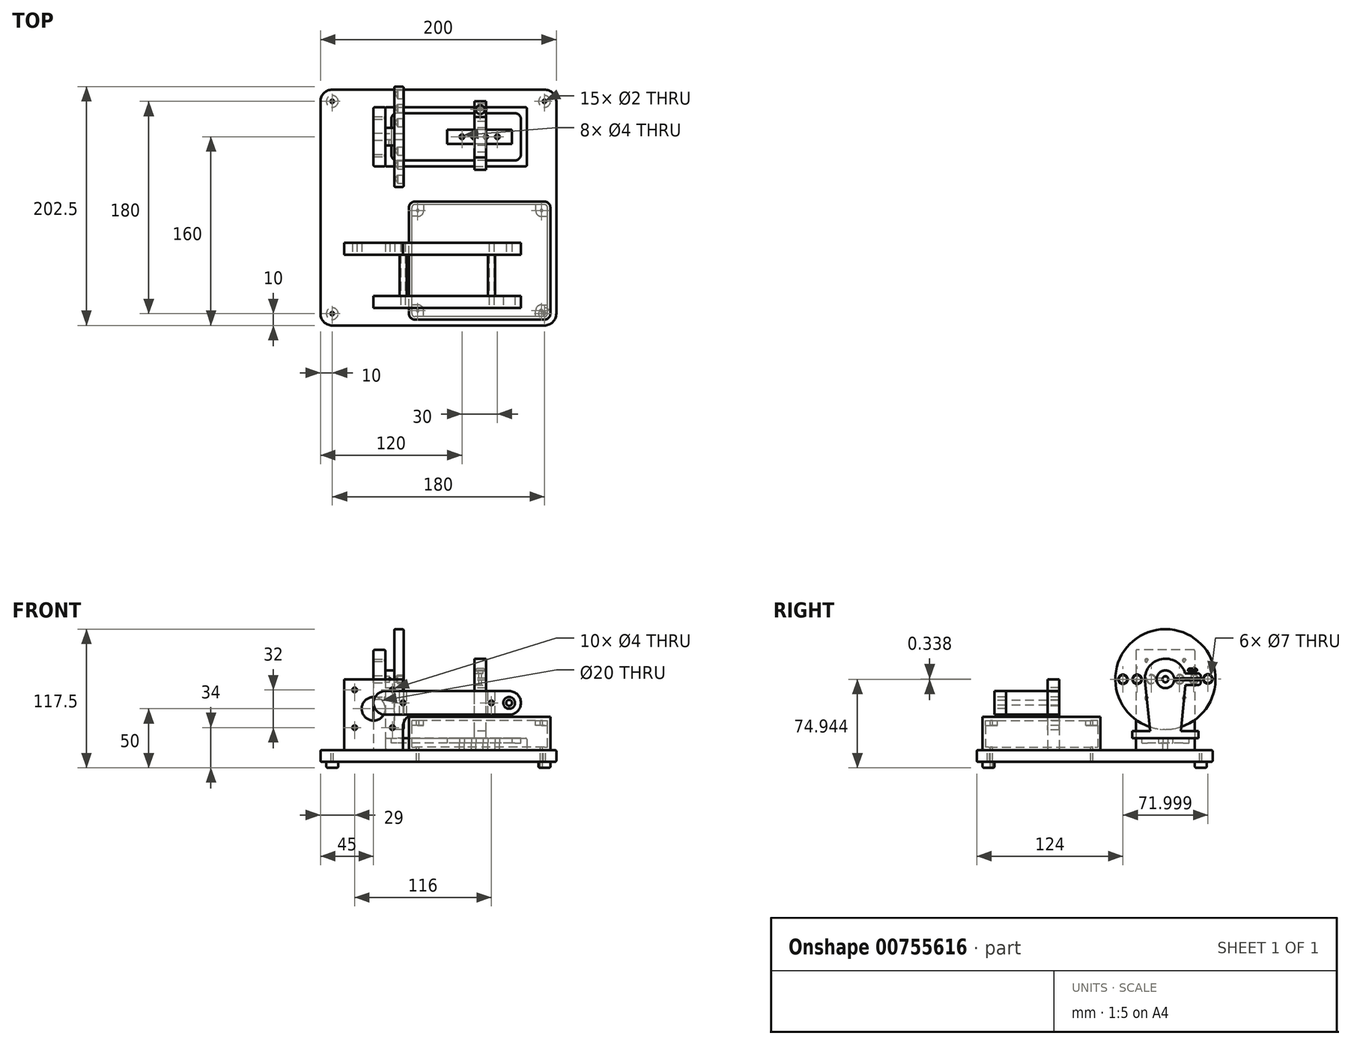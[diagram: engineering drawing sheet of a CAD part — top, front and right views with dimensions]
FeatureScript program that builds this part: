
annotation { "Feature Type Name" : "Feature", "Feature Type Description" : "" }
export const myFeature = defineFeature(function(context is Context, id is Id, definition is map)
    precondition{}
    {
        {
            var Q0;
            Q0=qCreatedBy(makeId("Top.planeOp"),FACE);
            var sketch = newSketch(context, id + "F0", { "sketchPlane" : qUnion([Q0])});
            skLineSegment(sketch, "E0.bottom", {"start": v(100, -100) * mm, "end": v(-100, -100) * mm});
            skLineSegment(sketch, "E0.top", {"start": v(100, 100) * mm, "end": v(-100, 100) * mm});
            skLineSegment(sketch, "E0.left", {"start": v(100, -100) * mm, "end": v(100, 100) * mm});
            skLineSegment(sketch, "E0.right", {"start": v(-100, -100) * mm, "end": v(-100, 100) * mm});
            skPoint(sketch, "E0.middle", {"position": v(0, 0) * mm});
            skSolve(sketch);
        }
        {
            var Q0;
            Q0=makeQuery(id+"F0.imprint","IMPRINT",FACE,{"disambiguationData":[TD([[makeQuery(id+"F0.imprint","IMPRINT",EDGE,{"derivedFrom":sQuery(id+"F0.wireOp",EDGE,"E0.bottom")}),-1.0]])]});
            extrude(context, id + "F1", {"entities" : qUnion([Q0]), "depth" : 10 * mm, "offsetDistance" : 25.4 * mm});
        }
        {
            var Q0;
            Q0=makeQuery(id+"F1.opExtrude","SWEPT_EDGE",EDGE,{"disambiguationData":[OSD([sQuery(id+"F0.wireOp",EDGE,"E0.bottom"),sQuery(id+"F0.wireOp",EDGE,"E0.left")])]});
            var Q1;
            Q1=makeQuery(id+"F1.opExtrude","SWEPT_EDGE",EDGE,{"disambiguationData":[OSD([sQuery(id+"F0.wireOp",EDGE,"E0.top"),sQuery(id+"F0.wireOp",EDGE,"E0.left")])]});
            var Q2;
            Q2=makeQuery(id+"F1.opExtrude","SWEPT_EDGE",EDGE,{"disambiguationData":[OSD([sQuery(id+"F0.wireOp",EDGE,"E0.top"),sQuery(id+"F0.wireOp",EDGE,"E0.right")])]});
            var Q3;
            Q3=makeQuery(id+"F1.opExtrude","SWEPT_EDGE",EDGE,{"disambiguationData":[OSD([sQuery(id+"F0.wireOp",EDGE,"E0.bottom"),sQuery(id+"F0.wireOp",EDGE,"E0.right")])]});
            fillet(context, id + "F2", {"entities" : qUnion([Q0, Q1, Q2, Q3]), "radius" : 10 * mm, "tangentPropagation" : true, "allowEdgeOverflow" : false});
        }
        {
            var Q0;
            Q0=makeQuery(id+"F1.opExtrude","CAP_FACE",FACE,{"disambiguationData":[OSD([sQuery(id+"F0.wireOp",EDGE,"E0.bottom"),sQuery(id+"F0.wireOp",EDGE,"E0.top"),sQuery(id+"F0.wireOp",EDGE,"E0.left"),sQuery(id+"F0.wireOp",EDGE,"E0.right")])],"isStart":false});
            var sketch = newSketch(context, id + "F3", { "sketchPlane" : qUnion([Q0])});
            skLineSegment(sketch, "E1.bottom", {"start": v(90, -90) * mm, "end": v(-90, -90) * mm, "construction": true});
            skLineSegment(sketch, "E1.top", {"start": v(90, 90) * mm, "end": v(-90, 90) * mm, "construction": true});
            skLineSegment(sketch, "E1.left", {"start": v(90, -90) * mm, "end": v(90, 90) * mm, "construction": true});
            skLineSegment(sketch, "E1.right", {"start": v(-90, -90) * mm, "end": v(-90, 90) * mm, "construction": true});
            skPoint(sketch, "E1.middle", {"position": v(0, 0) * mm});
            skSolve(sketch);
        }
        {
            var Q0;
            Q0=sQuery(id+"F3.wireOp",VERTEX,"E1.right.end");
            var Q1;
            Q1=sQuery(id+"F3.wireOp",VERTEX,"E1.left.end");
            var Q2;
            Q2=sQuery(id+"F3.wireOp",VERTEX,"E1.bottom.start");
            var Q3;
            Q3=sQuery(id+"F3.wireOp",VERTEX,"E1.right.start");
            var Q4;
            Q4=makeQuery(id+"F1.opExtrude","SWEPT_BODY",BODY,{"disambiguationData":[OSD([sQuery(id+"F0.wireOp",EDGE,"E0.bottom"),sQuery(id+"F0.wireOp",EDGE,"E0.top"),sQuery(id+"F0.wireOp",EDGE,"E0.left"),sQuery(id+"F0.wireOp",EDGE,"E0.right")])]});
            hole(context, id + "F4", {"style" : HoleStyle.C_SINK, "endStyle" : HoleEndStyle.THROUGH, "holeDiameter" : 2 * mm, "cSinkDiameter" : 3 * mm, "cSinkAngle" : 82 * degree, "majorDiameter" : 5 * mm, "isTappedThrough" : true, "tappedDepth" : 12 * mm, "tapClearance" : 3, "locations" : qUnion([Q0, Q1, Q2, Q3]), "scope" : qUnion([Q4])});
        }
        {
            var Q0;
            Q0=sQuery(id+"F3.wireOp",EDGE,"E1.left");
            var Q1;
            Q1=sQuery(id+"F3.wireOp",VERTEX,"E1.bottom.start");
            cPlane(context, id + "F5", {"entities" : qUnion([Q0, Q1]), "cplaneType" : CPlaneType.LINE_POINT, "offset" : 25 * mm, "width" : 150 * mm, "height" : 150 * mm});
        }
        {
            var Q0;
            Q0=qCreatedBy(id+"F5.planeOp",FACE);
            var sketch = newSketch(context, id + "F6", { "sketchPlane" : qUnion([Q0])});
            skLineSegment(sketch, "E2", {"start": v(-90, 10) * mm, "end": v(-90, -5) * mm, "construction": true});
            skLineSegment(sketch, "E3", {"start": v(-90, -5) * mm, "end": v(-95, -5) * mm});
            skLineSegment(sketch, "E4", {"start": v(-95, -5) * mm, "end": v(-95, 0) * mm});
            skLineSegment(sketch, "E5", {"start": v(-95, 0) * mm, "end": v(-90, 0) * mm});
            skLineSegment(sketch, "E6", {"start": v(-90, 0) * mm, "end": v(-90, -5) * mm});
            skSolve(sketch);
        }
        {
            var Q0;
            Q0=makeQuery(id+"F6.imprint","IMPRINT",FACE,{"disambiguationData":[TD([[makeQuery(id+"F6.imprint","IMPRINT",EDGE,{"derivedFrom":sQuery(id+"F6.wireOp",EDGE,"E3")}),-1.0]])]});
            var Q1;
            Q1=sQuery(id+"F6.wireOp",EDGE,"E6");
            revolve(context, id + "F7", {"surfaceOperationType" : NewSurfaceOperationType.NEW, "entities" : qUnion([Q0]), "axis" : qUnion([Q1]), "revolveType" : RevolveType.FULL});
        }
        {
            var Q0;
            Q0=makeQuery(id+"F7.opRevolve","SWEPT_EDGE",EDGE,{"disambiguationData":[OSD([sQuery(id+"F6.wireOp",EDGE,"E3"),sQuery(id+"F6.wireOp",EDGE,"E4")])]});
            fillet(context, id + "F8", {"entities" : qUnion([Q0]), "radius" : 1 * mm, "tangentPropagation" : true, "allowEdgeOverflow" : false});
        }
        {
            var Q0;
            Q0=makeQuery(id+"F7.opRevolve","SWEPT_BODY",BODY,{"disambiguationData":[OSD([sQuery(id+"F6.wireOp",EDGE,"E3"),sQuery(id+"F6.wireOp",EDGE,"E4"),sQuery(id+"F6.wireOp",EDGE,"E5"),sQuery(id+"F6.wireOp",EDGE,"E6")])]});
            var Q1;
            Q1=qCreatedBy(makeId("Right.planeOp"),FACE);
            mirror(context, id + "F9", {"entities" : qUnion([Q0]), "mirrorPlane" : qUnion([Q1])});
        }
        {
            var Q0;
            Q0=makeQuery(id+"F7.opRevolve","SWEPT_BODY",BODY,{"disambiguationData":[OSD([sQuery(id+"F6.wireOp",EDGE,"E3"),sQuery(id+"F6.wireOp",EDGE,"E4"),sQuery(id+"F6.wireOp",EDGE,"E5"),sQuery(id+"F6.wireOp",EDGE,"E6")])]});
            var Q1;
            Q1=makeQuery(id+"F9.opPattern","COPY",BODY,{"derivedFrom":makeQuery(id+"F7.opRevolve","SWEPT_BODY",BODY,{"disambiguationData":[OSD([sQuery(id+"F6.wireOp",EDGE,"E3"),sQuery(id+"F6.wireOp",EDGE,"E4"),sQuery(id+"F6.wireOp",EDGE,"E5"),sQuery(id+"F6.wireOp",EDGE,"E6")])]}),"instanceName":"1"});
            var Q2;
            Q2=qCreatedBy(makeId("Front.planeOp"),FACE);
            mirror(context, id + "F10", {"entities" : qUnion([Q0, Q1]), "mirrorPlane" : qUnion([Q2])});
        }
        {
            var Q0;
            Q0=makeQuery(id+"F1.opExtrude","CAP_EDGE",EDGE,{"disambiguationData":[OSD([sQuery(id+"F0.wireOp",EDGE,"E0.bottom")])],"isStart":false});
            var Q1;
            Q1=makeQuery(id+"F1.opExtrude","CAP_EDGE",EDGE,{"disambiguationData":[OSD([sQuery(id+"F0.wireOp",EDGE,"E0.bottom")])],"isStart":true});
            fillet(context, id + "F11", {"entities" : qUnion([Q0, Q1]), "radius" : 1 * mm, "tangentPropagation" : true, "allowEdgeOverflow" : false});
        }
        {
            var Q0;
            {var subQ3=sQuery(id+"F0.wireOp",EDGE,"E0.bottom");Q0=makeQuery(id+"F3.imprint","IMPRINT",FACE,{"disambiguationData":[TD([[makeQuery(id+"F3.imprint","IMPRINT",EDGE,{"derivedFrom":makeQuery(id+"F1.opExtrude","CAP_EDGE",EDGE,{"disambiguationData":[OSD([subQ3])],"isStart":false})}),-1.0]])]});}
            var sketch = newSketch(context, id + "F12", { "sketchPlane" : qUnion([Q0])});
            skLineSegment(sketch, "E7.bottom", {"start": v(-55, 85) * mm, "end": v(-45, 85) * mm});
            skLineSegment(sketch, "E7.top", {"start": v(-55, 35) * mm, "end": v(-45, 35) * mm});
            skLineSegment(sketch, "E7.left", {"start": v(-55, 85) * mm, "end": v(-55, 35) * mm});
            skLineSegment(sketch, "E7.right", {"start": v(-45, 85) * mm, "end": v(-45, 35) * mm});
            skSolve(sketch);
        }
        {
            var Q0;
            Q0=makeQuery(id+"F12.imprint","IMPRINT",FACE,{"disambiguationData":[TD([[makeQuery(id+"F12.imprint","IMPRINT",EDGE,{"derivedFrom":sQuery(id+"F12.wireOp",EDGE,"E7.bottom")}),-1.0]])]});
            extrude(context, id + "F13", {"entities" : qUnion([Q0]), "depth" : 85 * mm, "offsetDistance" : 25 * mm});
        }
        {
            var Q0;
            Q0=makeQuery(id+"F13.opExtrude","SWEPT_FACE",FACE,{"disambiguationData":[OSD([sQuery(id+"F12.wireOp",EDGE,"E7.right")])]});
            var sketch = newSketch(context, id + "F14", { "sketchPlane" : qUnion([Q0])});
            skLineSegment(sketch, "E8.bottom", {"start": v(76, 86) * mm, "end": v(44, 86) * mm, "construction": true});
            skLineSegment(sketch, "E8.top", {"start": v(76, 54) * mm, "end": v(44, 54) * mm, "construction": true});
            skLineSegment(sketch, "E8.left", {"start": v(76, 86) * mm, "end": v(76, 54) * mm, "construction": true});
            skLineSegment(sketch, "E8.right", {"start": v(44, 86) * mm, "end": v(44, 54) * mm, "construction": true});
            skPoint(sketch, "E8.middle", {"position": v(60, 70) * mm});
            skPoint(sketch, "E8.middle.positionSnap0", {"position": v(60, 95) * mm});
            skPoint(sketch, "E8.centerSnap0", {"position": v(60, 95) * mm});
            skSolve(sketch);
        }
        {
            var Q0;
            Q0=sQuery(id+"F14.wireOp",VERTEX,"E8.bottom.end");
            var Q1;
            Q1=sQuery(id+"F14.wireOp",VERTEX,"E8.right.end");
            var Q2;
            Q2=sQuery(id+"F14.wireOp",VERTEX,"E8.left.end");
            var Q3;
            Q3=sQuery(id+"F14.wireOp",VERTEX,"E8.left.start");
            var Q4;
            Q4=makeQuery(id+"F13.opExtrude","SWEPT_BODY",BODY,{"disambiguationData":[OSD([sQuery(id+"F12.wireOp",EDGE,"E7.bottom"),sQuery(id+"F12.wireOp",EDGE,"E7.top"),sQuery(id+"F12.wireOp",EDGE,"E7.left"),sQuery(id+"F12.wireOp",EDGE,"E7.right")])]});
            hole(context, id + "F15", {"style" : HoleStyle.C_SINK, "endStyle" : HoleEndStyle.THROUGH, "holeDiameter" : 2 * mm, "cSinkDiameter" : 3 * mm, "cSinkAngle" : 82 * degree, "majorDiameter" : 5 * mm, "isTappedThrough" : true, "tappedDepth" : 12 * mm, "tapClearance" : 3, "locations" : qUnion([Q0, Q1, Q2, Q3]), "scope" : qUnion([Q4])});
        }
        {
            var Q0;
            Q0=sQuery(id+"F14.wireOp",VERTEX,"E8.middle");
            var Q1;
            Q1=makeQuery(id+"F13.opExtrude","SWEPT_BODY",BODY,{"disambiguationData":[OSD([sQuery(id+"F12.wireOp",EDGE,"E7.bottom"),sQuery(id+"F12.wireOp",EDGE,"E7.top"),sQuery(id+"F12.wireOp",EDGE,"E7.left"),sQuery(id+"F12.wireOp",EDGE,"E7.right")])]});
            hole(context, id + "F16", {"style" : HoleStyle.SIMPLE, "endStyle" : HoleEndStyle.BLIND, "holeDiameter" : 6 * mm, "majorDiameter" : 5 * mm, "holeDepth" : 50.8 * mm, "isTappedThrough" : true, "tappedDepth" : 12 * mm, "tapClearance" : 3, "locations" : qUnion([Q0]), "scope" : qUnion([Q1])});
        }
        {
            var Q0;
            Q0=makeQuery(id+"F13.opExtrude","SWEPT_FACE",FACE,{"disambiguationData":[OSD([sQuery(id+"F12.wireOp",EDGE,"E7.top")])]});
            cPlane(context, id + "F17", {"entities" : qUnion([Q0]), "cplaneType" : CPlaneType.OFFSET, "offset" : 25 * mm, "oppositeDirection" : true, "width" : 150 * mm, "height" : 150 * mm});
        }
        {
            var Q0;
            Q0=qCreatedBy(id+"F17.planeOp",FACE);
            var sketch = newSketch(context, id + "F18", { "sketchPlane" : qUnion([Q0])});
            skLineSegment(sketch, "E9.bottom", {"start": v(-45, 62.5) * mm, "end": v(-52.5, 62.5) * mm, "construction": true});
            skLineSegment(sketch, "E9.top", {"start": v(-37.5, 77.5) * mm, "end": v(-52.5, 77.5) * mm, "construction": true});
            skLineSegment(sketch, "E9.left", {"start": v(-37.5, 62.5) * mm, "end": v(-37.5, 77.5) * mm, "construction": true});
            skLineSegment(sketch, "E9.right", {"start": v(-52.5, 62.5) * mm, "end": v(-52.5, 77.5) * mm, "construction": true});
            skPoint(sketch, "E9.middle", {"position": v(-45, 70) * mm});
            skLineSegment(sketch, "E10", {"start": v(-37.5, 77.5) * mm, "end": v(-45, 77.5) * mm});
            skLineSegment(sketch, "E11", {"start": v(-45, 77.5) * mm, "end": v(-45, 70) * mm});
            skLineSegment(sketch, "E12", {"start": v(-45, 62.5) * mm, "end": v(-37.5, 62.5) * mm});
            skLineSegment(sketch, "E13", {"start": v(-37.5, 77.5) * mm, "end": v(-37.5, 112.5) * mm});
            skLineSegment(sketch, "E14", {"start": v(-37.5, 112.5) * mm, "end": v(-29.5, 112.5) * mm});
            skLineSegment(sketch, "E15", {"start": v(-29.5, 112.5) * mm, "end": v(-29.5, 70) * mm});
            skLineSegment(sketch, "E16", {"start": v(-45, 70) * mm, "end": v(-29.5, 70) * mm});
            skPoint(sketch, "E17.end.orphan", {"position": v(-35, 27.5) * mm});
            skPoint(sketch, "E17.start.orphan", {"position": v(-29.5, 27.5) * mm});
            skSolve(sketch);
        }
        {
            var Q0;
            Q0=makeQuery(id+"F18.imprint","IMPRINT",FACE,{"disambiguationData":[TD([[makeQuery(id+"F18.imprint","IMPRINT",EDGE,{"derivedFrom":sQuery(id+"F18.wireOp",EDGE,"E10")}),1.0]])]});
            var Q1;
            Q1=sQuery(id+"F18.wireOp",EDGE,"E16");
            revolve(context, id + "F19", {"surfaceOperationType" : NewSurfaceOperationType.NEW, "entities" : qUnion([Q0]), "axis" : qUnion([Q1]), "revolveType" : RevolveType.FULL});
        }
        {
            var Q0;
            Q0=sQuery(id+"F14.wireOp",VERTEX,"E8.middle");
            var Q1;
            Q1=makeQuery(id+"F19.opRevolve","SWEPT_BODY",BODY,{"disambiguationData":[OSD([sQuery(id+"F18.wireOp",EDGE,"E10"),sQuery(id+"F18.wireOp",EDGE,"E11"),sQuery(id+"F18.wireOp",EDGE,"E13"),sQuery(id+"F18.wireOp",EDGE,"E14"),sQuery(id+"F18.wireOp",EDGE,"E15"),sQuery(id+"F18.wireOp",EDGE,"E16")])]});
            hole(context, id + "F20", {"style" : HoleStyle.SIMPLE, "endStyle" : HoleEndStyle.BLIND, "oppositeDirection" : true, "holeDiameter" : 5 * mm, "majorDiameter" : 5 * mm, "holeDepth" : 50.8 * mm, "isTappedThrough" : true, "tappedDepth" : 12 * mm, "tapClearance" : 3, "locations" : qUnion([Q0]), "scope" : qUnion([Q1])});
        }
        {
            var Q0;
            Q0=makeQuery(id+"F19.opRevolve","SWEPT_FACE",FACE,{"disambiguationData":[OSD([sQuery(id+"F18.wireOp",EDGE,"E15")])]});
            var sketch = newSketch(context, id + "F21", { "sketchPlane" : qUnion([Q0])});
            skLineSegment(sketch, "E18", {"start": v(48, 69.94) * mm, "end": v(60, 70) * mm, "construction": true});
            skLineSegment(sketch, "E19", {"start": v(48, 69.94) * mm, "end": v(36, 69.94) * mm, "construction": true});
            skLineSegment(sketch, "E20", {"start": v(36, 69.94) * mm, "end": v(24, 69.94) * mm, "construction": true});
            skLineSegment(sketch, "E21", {"start": v(60, 70) * mm, "end": v(59.93, 85.7) * mm, "construction": true});
            skLineSegment(sketch, "E22.MirrorCS", {"start": v(72, 70.06) * mm, "end": v(60, 70) * mm, "construction": true});
            skLineSegment(sketch, "E23.MirrorCS", {"start": v(72, 70.06) * mm, "end": v(84, 70.17) * mm, "construction": true});
            skLineSegment(sketch, "E24.MirrorCS", {"start": v(84, 70.17) * mm, "end": v(96, 70.28) * mm, "construction": true});
            skSolve(sketch);
        }
        {
            var Q0;
            Q0=sQuery(id+"F21.wireOp",VERTEX,"E20.end");
            var Q1;
            Q1=sQuery(id+"F21.wireOp",VERTEX,"E18.start");
            var Q2;
            Q2=sQuery(id+"F21.wireOp",VERTEX,"E23.MirrorCS.start");
            var Q3;
            Q3=sQuery(id+"F21.wireOp",VERTEX,"E24.MirrorCS.start");
            var Q4;
            Q4=sQuery(id+"F21.wireOp",VERTEX,"E24.MirrorCS.end");
            var Q5;
            Q5=sQuery(id+"F21.wireOp",VERTEX,"E19.end");
            var Q6;
            Q6=makeQuery(id+"F19.opRevolve","SWEPT_BODY",BODY,{"disambiguationData":[OSD([sQuery(id+"F18.wireOp",EDGE,"E10"),sQuery(id+"F18.wireOp",EDGE,"E11"),sQuery(id+"F18.wireOp",EDGE,"E13"),sQuery(id+"F18.wireOp",EDGE,"E14"),sQuery(id+"F18.wireOp",EDGE,"E15"),sQuery(id+"F18.wireOp",EDGE,"E16")])]});
            hole(context, id + "F22", {"style" : HoleStyle.C_SINK, "endStyle" : HoleEndStyle.BLIND, "holeDiameter" : 7 * mm, "cSinkDiameter" : 8 * mm, "cSinkAngle" : 82 * degree, "majorDiameter" : 5 * mm, "holeDepth" : 5 * mm, "isTappedThrough" : true, "tappedDepth" : 12 * mm, "tapClearance" : 3, "locations" : qUnion([Q0, Q1, Q2, Q3, Q4, Q5]), "scope" : qUnion([Q6])});
        }
        {
            var Q0;
            Q0=qCreatedBy(id+"F17.planeOp",FACE);
            var sketch = newSketch(context, id + "F23", { "sketchPlane" : qUnion([Q0])});
            skLineSegment(sketch, "E25", {"start": v(-45, 70) * mm, "end": v(-41.25, 70) * mm, "construction": true});
            skSolve(sketch);
        }
        {
            var Q0;
            Q0=qCreatedBy(id+"F17.planeOp",FACE);
            cPlane(context, id + "F24", {"entities" : qUnion([Q0]), "cplaneType" : CPlaneType.OFFSET, "offset" : 10 * mm, "width" : 150 * mm, "height" : 150 * mm});
        }
        {
            var Q0;
            Q0=qCreatedBy(id+"F24.planeOp",FACE);
            var sketch = newSketch(context, id + "F25", { "sketchPlane" : qUnion([Q0])});
            skPoint(sketch, "E26", {"position": v(-41.25, 70) * mm});
            skSolve(sketch);
        }
        {
            var Q0;
            Q0=sQuery(id+"F25.wireOp",VERTEX,"E26");
            var Q1;
            Q1=makeQuery(id+"F19.opRevolve","SWEPT_BODY",BODY,{"disambiguationData":[OSD([sQuery(id+"F18.wireOp",EDGE,"E10"),sQuery(id+"F18.wireOp",EDGE,"E11"),sQuery(id+"F18.wireOp",EDGE,"E13"),sQuery(id+"F18.wireOp",EDGE,"E14"),sQuery(id+"F18.wireOp",EDGE,"E15"),sQuery(id+"F18.wireOp",EDGE,"E16")])]});
            hole(context, id + "F26", {"style" : HoleStyle.SIMPLE, "endStyle" : HoleEndStyle.BLIND, "holeDiameter" : 2 * mm, "majorDiameter" : 5 * mm, "holeDepth" : 5 * mm, "isTappedThrough" : true, "tappedDepth" : 12 * mm, "tapClearance" : 3, "locations" : qUnion([Q0]), "scope" : qUnion([Q1])});
        }
        {
            var Q0;
            Q0=makeQuery(id+"F19.opRevolve","SWEPT_EDGE",EDGE,{"disambiguationData":[OSD([sQuery(id+"F18.wireOp",EDGE,"E14"),sQuery(id+"F18.wireOp",EDGE,"E15")])]});
            var Q1;
            Q1=makeQuery(id+"F19.opRevolve","SWEPT_EDGE",EDGE,{"disambiguationData":[OSD([sQuery(id+"F18.wireOp",EDGE,"E13"),sQuery(id+"F18.wireOp",EDGE,"E14")])]});
            fillet(context, id + "F27", {"entities" : qUnion([Q0, Q1]), "radius" : 1 * mm, "tangentPropagation" : true, "allowEdgeOverflow" : false});
        }
        {
            var Q0;
            Q0=makeQuery(id+"F13.opExtrude","SWEPT_EDGE",EDGE,{"disambiguationData":[OSD([sQuery(id+"F12.wireOp",EDGE,"E7.top"),sQuery(id+"F12.wireOp",EDGE,"E7.right")])]});
            var Q1;
            Q1=makeQuery(id+"F13.opExtrude","SWEPT_EDGE",EDGE,{"disambiguationData":[OSD([sQuery(id+"F12.wireOp",EDGE,"E7.top"),sQuery(id+"F12.wireOp",EDGE,"E7.left")])]});
            var Q2;
            Q2=makeQuery(id+"F13.opExtrude","SWEPT_EDGE",EDGE,{"disambiguationData":[OSD([sQuery(id+"F12.wireOp",EDGE,"E7.bottom"),sQuery(id+"F12.wireOp",EDGE,"E7.left")])]});
            var Q3;
            Q3=makeQuery(id+"F13.opExtrude","SWEPT_EDGE",EDGE,{"disambiguationData":[OSD([sQuery(id+"F12.wireOp",EDGE,"E7.bottom"),sQuery(id+"F12.wireOp",EDGE,"E7.right")])]});
            var Q4;
            Q4=makeQuery(id+"F13.opExtrude","CAP_EDGE",EDGE,{"disambiguationData":[OSD([sQuery(id+"F12.wireOp",EDGE,"E7.bottom")])],"isStart":false});
            var Q5;
            Q5=makeQuery(id+"F13.opExtrude","CAP_EDGE",EDGE,{"disambiguationData":[OSD([sQuery(id+"F12.wireOp",EDGE,"E7.left")])],"isStart":false});
            var Q6;
            Q6=makeQuery(id+"F13.opExtrude","CAP_EDGE",EDGE,{"disambiguationData":[OSD([sQuery(id+"F12.wireOp",EDGE,"E7.right")])],"isStart":false});
            var Q7;
            Q7=makeQuery(id+"F13.opExtrude","CAP_EDGE",EDGE,{"disambiguationData":[OSD([sQuery(id+"F12.wireOp",EDGE,"E7.top")])],"isStart":false});
            fillet(context, id + "F28", {"entities" : qUnion([Q0, Q1, Q2, Q3, Q4, Q5, Q6, Q7]), "radius" : 1 * mm, "tangentPropagation" : true, "allowEdgeOverflow" : false});
        }
        {
            var Q0;
            Q0=makeQuery(id+"F12.imprint","IMPRINT",FACE,{"disambiguationData":[TD([[makeQuery(id+"F12.imprint","IMPRINT",EDGE,{"derivedFrom":sQuery(id+"F12.wireOp",EDGE,"E7.bottom")}),1.0]])]});
            var sketch = newSketch(context, id + "F29", { "sketchPlane" : qUnion([Q0])});
            skLineSegment(sketch, "E27.bottom", {"start": v(-45, 85) * mm, "end": v(75, 85) * mm});
            skLineSegment(sketch, "E27.top", {"start": v(-45, 35) * mm, "end": v(75, 35) * mm});
            skLineSegment(sketch, "E27.left", {"start": v(-45, 85) * mm, "end": v(-45, 35) * mm});
            skLineSegment(sketch, "E27.right", {"start": v(75, 85) * mm, "end": v(75, 35) * mm});
            skSolve(sketch);
        }
        {
            var Q0;
            Q0 = qSketchRegion(id + "F29", true);
            extrude(context, id + "F30", {"entities" : qUnion([Q0]), "depth" : 10 * mm, "offsetDistance" : 25 * mm});
        }
        {
            var Q0;
            Q0=makeQuery(id+"F30.opExtrude","CAP_FACE",FACE,{"disambiguationData":[OSD([sQuery(id+"F29.wireOp",EDGE,"E27.bottom"),sQuery(id+"F29.wireOp",EDGE,"E27.top"),sQuery(id+"F29.wireOp",EDGE,"E27.left"),sQuery(id+"F29.wireOp",EDGE,"E27.right")])],"isStart":false});
            var sketch = newSketch(context, id + "F31", { "sketchPlane" : qUnion([Q0])});
            skLineSegment(sketch, "E28.bottom", {"start": v(70, 80) * mm, "end": v(-40, 80) * mm});
            skLineSegment(sketch, "E28.top", {"start": v(70, 40) * mm, "end": v(-40, 40) * mm});
            skLineSegment(sketch, "E28.left", {"start": v(70, 80) * mm, "end": v(70, 40) * mm});
            skLineSegment(sketch, "E28.right", {"start": v(-40, 80) * mm, "end": v(-40, 40) * mm});
            skSolve(sketch);
        }
        {
            var Q0;
            Q0=makeQuery(id+"F31.imprint","IMPRINT",FACE,{"disambiguationData":[TD([[makeQuery(id+"F31.imprint","IMPRINT",EDGE,{"derivedFrom":sQuery(id+"F31.wireOp",EDGE,"E28.bottom")}),1.0]])]});
            extrude(context, id + "F32", {"entities" : qUnion([Q0]), "operationType" : NewBodyOperationType.REMOVE, "oppositeDirection" : true, "depth" : 4 * mm, "offsetDistance" : 25 * mm});
        }
        {
            var Q0;
            Q0=makeQuery(id+"F32.boolean.opBoolean","COPY",EDGE,{"derivedFrom":makeQuery(id+"F32.opExtrude","SWEPT_EDGE",EDGE,{"disambiguationData":[OSD([sQuery(id+"F31.wireOp",EDGE,"E28.top"),sQuery(id+"F31.wireOp",EDGE,"E28.right")])]})});
            var Q1;
            Q1=makeQuery(id+"F32.boolean.opBoolean","COPY",EDGE,{"derivedFrom":makeQuery(id+"F32.opExtrude","SWEPT_EDGE",EDGE,{"disambiguationData":[OSD([sQuery(id+"F31.wireOp",EDGE,"E28.bottom"),sQuery(id+"F31.wireOp",EDGE,"E28.right")])]})});
            var Q2;
            Q2=makeQuery(id+"F32.boolean.opBoolean","COPY",EDGE,{"derivedFrom":makeQuery(id+"F32.opExtrude","SWEPT_EDGE",EDGE,{"disambiguationData":[OSD([sQuery(id+"F31.wireOp",EDGE,"E28.bottom"),sQuery(id+"F31.wireOp",EDGE,"E28.left")])]})});
            var Q3;
            Q3=makeQuery(id+"F32.boolean.opBoolean","COPY",EDGE,{"derivedFrom":makeQuery(id+"F32.opExtrude","SWEPT_EDGE",EDGE,{"disambiguationData":[OSD([sQuery(id+"F31.wireOp",EDGE,"E28.top"),sQuery(id+"F31.wireOp",EDGE,"E28.left")])]})});
            fillet(context, id + "F33", {"entities" : qUnion([Q0, Q1, Q2, Q3]), "radius" : 5 * mm, "tangentPropagation" : true, "allowEdgeOverflow" : false});
        }
        {
            var Q0;
            Q0=makeQuery(id+"F30.opExtrude","SWEPT_EDGE",EDGE,{"disambiguationData":[OSD([sQuery(id+"F29.wireOp",EDGE,"E27.bottom"),sQuery(id+"F29.wireOp",EDGE,"E27.right")])]});
            var Q1;
            Q1=makeQuery(id+"F30.opExtrude","CAP_EDGE",EDGE,{"disambiguationData":[OSD([sQuery(id+"F29.wireOp",EDGE,"E27.right")])],"isStart":false});
            var Q2;
            Q2=makeQuery(id+"F30.opExtrude","SWEPT_EDGE",EDGE,{"disambiguationData":[OSD([sQuery(id+"F29.wireOp",EDGE,"E27.top"),sQuery(id+"F29.wireOp",EDGE,"E27.right")])]});
            var Q3;
            Q3=makeQuery(id+"F30.opExtrude","CAP_EDGE",EDGE,{"disambiguationData":[OSD([sQuery(id+"F29.wireOp",EDGE,"E27.bottom")])],"isStart":false});
            var Q4;
            Q4=makeQuery(id+"F30.opExtrude","CAP_EDGE",EDGE,{"disambiguationData":[OSD([sQuery(id+"F29.wireOp",EDGE,"E27.top")])],"isStart":false});
            var Q5;
            Q5=makeQuery(id+"F32.boolean.opBoolean","COPY",EDGE,{"derivedFrom":makeQuery(id+"F32.opExtrude","CAP_EDGE",EDGE,{"disambiguationData":[OSD([sQuery(id+"F31.wireOp",EDGE,"E28.top")])],"isStart":true})});
            var Q6;
            Q6=makeQuery(id+"F30.opExtrude","SWEPT_EDGE",EDGE,{"disambiguationData":[OSD([sQuery(id+"F12.wireOp",EDGE,"E7.top"),sQuery(id+"F29.wireOp",EDGE,"E27.top"),sQuery(id+"F29.wireOp",EDGE,"E27.left")])]});
            var Q7;
            Q7=makeQuery(id+"F30.opExtrude","CAP_EDGE",EDGE,{"disambiguationData":[OSD([sQuery(id+"F29.wireOp",EDGE,"E27.top")])],"isStart":true});
            var Q8;
            Q8=makeQuery(id+"F30.opExtrude","CAP_EDGE",EDGE,{"disambiguationData":[OSD([sQuery(id+"F29.wireOp",EDGE,"E27.right")])],"isStart":true});
            var Q9;
            Q9=makeQuery(id+"F30.opExtrude","SWEPT_EDGE",EDGE,{"disambiguationData":[OSD([sQuery(id+"F12.wireOp",EDGE,"E7.bottom"),sQuery(id+"F29.wireOp",EDGE,"E27.bottom"),sQuery(id+"F29.wireOp",EDGE,"E27.left")])]});
            var Q10;
            Q10=makeQuery(id+"F30.opExtrude","CAP_EDGE",EDGE,{"disambiguationData":[OSD([sQuery(id+"F29.wireOp",EDGE,"E27.bottom")])],"isStart":true});
            var Q11;
            Q11=makeQuery(id+"F30.opExtrude","CAP_EDGE",EDGE,{"disambiguationData":[OSD([sQuery(id+"F29.wireOp",EDGE,"E27.left")])],"isStart":false});
            fillet(context, id + "F34", {"entities" : qUnion([Q0, Q1, Q2, Q3, Q4, Q5, Q6, Q7, Q8, Q9, Q10, Q11]), "radius" : 1 * mm, "tangentPropagation" : true, "allowEdgeOverflow" : false});
        }
        {
            var Q0;
            Q0=makeQuery(id+"F32.boolean.opBoolean","COPY",FACE,{"derivedFrom":makeQuery(id+"F32.opExtrude","CAP_FACE",FACE,{"disambiguationData":[OSD([sQuery(id+"F31.wireOp",EDGE,"E28.bottom"),sQuery(id+"F31.wireOp",EDGE,"E28.top"),sQuery(id+"F31.wireOp",EDGE,"E28.left"),sQuery(id+"F31.wireOp",EDGE,"E28.right")])],"isStart":false})});
            var sketch = newSketch(context, id + "F35", { "sketchPlane" : qUnion([Q0])});
            skLineSegment(sketch, "E29", {"start": v(70, 60) * mm, "end": v(50, 60) * mm, "construction": true});
            skLineSegment(sketch, "E30", {"start": v(50, 60) * mm, "end": v(40, 60) * mm, "construction": true});
            skLineSegment(sketch, "E31", {"start": v(40, 60) * mm, "end": v(30, 60) * mm, "construction": true});
            skLineSegment(sketch, "E32", {"start": v(30, 60) * mm, "end": v(20, 60) * mm, "construction": true});
            skSolve(sketch);
        }
        {
            var Q0;
            Q0=sQuery(id+"F35.wireOp",VERTEX,"E29.end");
            var Q1;
            Q1=sQuery(id+"F35.wireOp",VERTEX,"E30.end");
            var Q2;
            Q2=sQuery(id+"F35.wireOp",VERTEX,"E31.end");
            var Q3;
            Q3=sQuery(id+"F35.wireOp",VERTEX,"E32.end");
            var Q4;
            Q4=makeQuery(id+"F30.opExtrude","SWEPT_BODY",BODY,{"disambiguationData":[OSD([sQuery(id+"F29.wireOp",EDGE,"E27.bottom"),sQuery(id+"F29.wireOp",EDGE,"E27.top"),sQuery(id+"F29.wireOp",EDGE,"E27.left"),sQuery(id+"F29.wireOp",EDGE,"E27.right")])]});
            hole(context, id + "F36", {"style" : HoleStyle.SIMPLE, "endStyle" : HoleEndStyle.THROUGH, "holeDiameter" : 4 * mm, "majorDiameter" : 5 * mm, "isTappedThrough" : true, "tappedDepth" : 12 * mm, "tapClearance" : 3, "locations" : qUnion([Q0, Q1, Q2, Q3]), "scope" : qUnion([Q4])});
        }
        {
            var Q0;
            Q0=makeQuery(id+"F32.boolean.opBoolean","COPY",FACE,{"derivedFrom":makeQuery(id+"F32.opExtrude","CAP_FACE",FACE,{"disambiguationData":[OSD([sQuery(id+"F31.wireOp",EDGE,"E28.bottom"),sQuery(id+"F31.wireOp",EDGE,"E28.top"),sQuery(id+"F31.wireOp",EDGE,"E28.left"),sQuery(id+"F31.wireOp",EDGE,"E28.right")])],"isStart":false})});
            var sketch = newSketch(context, id + "F37", { "sketchPlane" : qUnion([Q0])});
            skLineSegment(sketch, "E33.bottom", {"start": v(62.5, 54) * mm, "end": v(7.5, 54) * mm});
            skLineSegment(sketch, "E33.top", {"start": v(62.5, 66) * mm, "end": v(7.5, 66) * mm});
            skLineSegment(sketch, "E33.left", {"start": v(62.5, 54) * mm, "end": v(62.5, 66) * mm});
            skLineSegment(sketch, "E33.right", {"start": v(7.5, 54) * mm, "end": v(7.5, 66) * mm});
            skPoint(sketch, "E33.middle", {"position": v(35, 60) * mm});
            skLineSegment(sketch, "E34", {"start": v(40, 60) * mm, "end": v(30, 60) * mm, "construction": true});
            skSolve(sketch);
        }
        {
            var Q0;
            Q0=makeQuery(id+"F37.imprint","IMPRINT",FACE,{"disambiguationData":[TD([[makeQuery(id+"F37.imprint","IMPRINT",EDGE,{"derivedFrom":sQuery(id+"F37.wireOp",EDGE,"E33.bottom")}),-1.0]])]});
            extrude(context, id + "F38", {"entities" : qUnion([Q0]), "depth" : 4 * mm, "offsetDistance" : 25 * mm});
        }
        {
            var Q0;
            Q0=makeQuery(id+"F12.imprint","IMPRINT",FACE,{"disambiguationData":[TD([[makeQuery(id+"F12.imprint","IMPRINT",EDGE,{"derivedFrom":sQuery(id+"F12.wireOp",EDGE,"E7.bottom")}),1.0]])]});
            var sketch = newSketch(context, id + "F39", { "sketchPlane" : qUnion([Q0])});
            skLineSegment(sketch, "E35.bottom", {"start": v(-30, -40) * mm, "end": v(-80, -40) * mm});
            skLineSegment(sketch, "E35.top", {"start": v(-30, -30) * mm, "end": v(-80, -30) * mm});
            skLineSegment(sketch, "E35.left", {"start": v(-30, -40) * mm, "end": v(-30, -30) * mm});
            skLineSegment(sketch, "E35.right", {"start": v(-80, -40) * mm, "end": v(-80, -30) * mm});
            skPoint(sketch, "E35.middle", {"position": v(-55, -35) * mm});
            skSolve(sketch);
        }
        {
            var Q0;
            Q0=makeQuery(id+"F39.imprint","IMPRINT",FACE,{"disambiguationData":[TD([[makeQuery(id+"F39.imprint","IMPRINT",EDGE,{"derivedFrom":sQuery(id+"F39.wireOp",EDGE,"E35.bottom")}),-1.0]])]});
            extrude(context, id + "F40", {"entities" : qUnion([Q0]), "depth" : 60 * mm, "offsetDistance" : 25 * mm});
        }
        {
            var Q0;
            Q0=makeQuery(id+"F40.opExtrude","SWEPT_FACE",FACE,{"disambiguationData":[OSD([sQuery(id+"F39.wireOp",EDGE,"E35.bottom")])]});
            var sketch = newSketch(context, id + "F41", { "sketchPlane" : qUnion([Q0])});
            skLineSegment(sketch, "E36.bottom", {"start": v(-39, 61) * mm, "end": v(-71, 61) * mm, "construction": true});
            skLineSegment(sketch, "E36.top", {"start": v(-39, 29) * mm, "end": v(-71, 29) * mm, "construction": true});
            skLineSegment(sketch, "E36.left", {"start": v(-39, 61) * mm, "end": v(-39, 29) * mm, "construction": true});
            skLineSegment(sketch, "E36.right", {"start": v(-71, 61) * mm, "end": v(-71, 29) * mm, "construction": true});
            skPoint(sketch, "E36.middle", {"position": v(-55, 45) * mm});
            skPoint(sketch, "E36.middle.positionSnap0", {"position": v(-55, 70) * mm});
            skPoint(sketch, "E36.centerSnap0", {"position": v(-55, 70) * mm});
            skSolve(sketch);
        }
        {
            var Q0;
            Q0=sQuery(id+"F41.wireOp",VERTEX,"E36.right.start");
            var Q1;
            Q1=sQuery(id+"F41.wireOp",VERTEX,"E36.left.start");
            var Q2;
            Q2=sQuery(id+"F41.wireOp",VERTEX,"E36.left.end");
            var Q3;
            Q3=sQuery(id+"F41.wireOp",VERTEX,"E36.right.end");
            var Q4;
            Q4=makeQuery(id+"F40.opExtrude","SWEPT_BODY",BODY,{"disambiguationData":[OSD([sQuery(id+"F39.wireOp",EDGE,"E35.bottom"),sQuery(id+"F39.wireOp",EDGE,"E35.top"),sQuery(id+"F39.wireOp",EDGE,"E35.left"),sQuery(id+"F39.wireOp",EDGE,"E35.right")])]});
            hole(context, id + "F42", {"style" : HoleStyle.SIMPLE, "endStyle" : HoleEndStyle.THROUGH, "holeDiameter" : 4 * mm, "majorDiameter" : 5 * mm, "isTappedThrough" : true, "tappedDepth" : 12 * mm, "tapClearance" : 3, "locations" : qUnion([Q0, Q1, Q2, Q3]), "scope" : qUnion([Q4])});
        }
        {
            var Q0;
            Q0=sQuery(id+"F41.wireOp",VERTEX,"E36.middle");
            var Q1;
            Q1=makeQuery(id+"F40.opExtrude","SWEPT_BODY",BODY,{"disambiguationData":[OSD([sQuery(id+"F39.wireOp",EDGE,"E35.bottom"),sQuery(id+"F39.wireOp",EDGE,"E35.top"),sQuery(id+"F39.wireOp",EDGE,"E35.left"),sQuery(id+"F39.wireOp",EDGE,"E35.right")])]});
            hole(context, id + "F43", {"style" : HoleStyle.SIMPLE, "endStyle" : HoleEndStyle.BLIND, "holeDiameter" : 20 * mm, "majorDiameter" : 5 * mm, "holeDepth" : 10 * mm, "isTappedThrough" : true, "tappedDepth" : 12 * mm, "tapClearance" : 3, "locations" : qUnion([Q0]), "scope" : qUnion([Q1])});
        }
        {
            var Q0;
            Q0=makeQuery(id+"F40.opExtrude","SWEPT_FACE",FACE,{"disambiguationData":[OSD([sQuery(id+"F39.wireOp",EDGE,"E35.left")])]});
            var sketch = newSketch(context, id + "F44", { "sketchPlane" : qUnion([Q0])});
            skLineSegment(sketch, "E37.bottom", {"start": v(-40, 60) * mm, "end": v(-30, 60) * mm});
            skLineSegment(sketch, "E37.top", {"start": v(-40, 40) * mm, "end": v(-30, 40) * mm});
            skLineSegment(sketch, "E37.left", {"start": v(-40, 60) * mm, "end": v(-40, 40) * mm});
            skLineSegment(sketch, "E37.right", {"start": v(-30, 60) * mm, "end": v(-30, 40) * mm});
            skPoint(sketch, "E37.middle", {"position": v(-35, 50) * mm});
            skPoint(sketch, "E37.middle.positionSnap0", {"position": v(-35, 70) * mm});
            skPoint(sketch, "E37.centerSnap0", {"position": v(-35, 70) * mm});
            skSolve(sketch);
        }
        {
            var Q0;
            Q0=makeQuery(id+"F44.imprint","IMPRINT",FACE,{"disambiguationData":[TD([[makeQuery(id+"F44.imprint","IMPRINT",EDGE,{"derivedFrom":sQuery(id+"F44.wireOp",EDGE,"E37.bottom")}),-1.0]])]});
            extrude(context, id + "F45", {"entities" : qUnion([Q0]), "operationType" : NewBodyOperationType.ADD, "depth" : 100 * mm, "offsetDistance" : 25 * mm});
        }
        {
            var Q0;
            Q0=makeQuery(id+"F45.opExtrude","CAP_EDGE",EDGE,{"disambiguationData":[OSD([sQuery(id+"F44.wireOp",EDGE,"E37.bottom")])],"isStart":true});
            var Q1;
            Q1=makeQuery(id+"F45.opExtrude","CAP_EDGE",EDGE,{"disambiguationData":[OSD([sQuery(id+"F44.wireOp",EDGE,"E37.bottom")])],"isStart":false});
            var Q2;
            Q2=makeQuery(id+"F45.opExtrude","CAP_EDGE",EDGE,{"disambiguationData":[OSD([sQuery(id+"F44.wireOp",EDGE,"E37.top")])],"isStart":false});
            var Q3;
            Q3=makeQuery(id+"F45.opExtrude","CAP_EDGE",EDGE,{"disambiguationData":[OSD([sQuery(id+"F44.wireOp",EDGE,"E37.top")])],"isStart":true});
            fillet(context, id + "F46", {"entities" : qUnion([Q0, Q1, Q2, Q3]), "radius" : 10 * mm, "tangentPropagation" : true, "allowEdgeOverflow" : false});
        }
        {
            var Q0;
            Q0=makeQuery(id+"F45.boolean.opBoolean","MERGE",FACE,{"derivedFrom":[makeQuery(id+"F40.opExtrude","SWEPT_FACE",FACE,{"disambiguationData":[OSD([sQuery(id+"F39.wireOp",EDGE,"E35.bottom")])]}),makeQuery(id+"F45.opExtrude","SWEPT_FACE",FACE,{"disambiguationData":[OSD([sQuery(id+"F44.wireOp",EDGE,"E37.left")])]})]});
            cPlane(context, id + "F47", {"entities" : qUnion([Q0]), "cplaneType" : CPlaneType.OFFSET, "offset" : 40 * mm, "width" : 150 * mm, "height" : 150 * mm});
        }
        {
            var Q0;
            Q0=qCreatedBy(id+"F47.planeOp",FACE);
            var sketch = newSketch(context, id + "F48", { "sketchPlane" : qUnion([Q0])});
            skLineSegment(sketch, "E38.0", {"start": v(70, 60) * mm, "end": v(-55, 60) * mm});
            skLineSegment(sketch, "E39.0", {"start": v(70, 40) * mm, "end": v(-55, 40) * mm});
            skLineSegment(sketch, "E40", {"start": v(-55, 45) * mm, "end": v(-55, 60) * mm});
            skLineSegment(sketch, "E41", {"start": v(-55, 45) * mm, "end": v(-55, 40) * mm});
            skLineSegment(sketch, "E42", {"start": v(70, 60) * mm, "end": v(70, 40) * mm});
            skSolve(sketch);
        }
        {
            var Q0;
            Q0=makeQuery(id+"F48.imprint","IMPRINT",FACE,{"disambiguationData":[TD([[makeQuery(id+"F48.imprint","IMPRINT",EDGE,{"derivedFrom":sQuery(id+"F48.wireOp",EDGE,"E38.0")}),1.0]])]});
            extrude(context, id + "F49", {"entities" : qUnion([Q0]), "endBound" : BoundingType.SYMMETRIC, "depth" : 10 * mm, "offsetDistance" : 25 * mm});
        }
        {
            var Q0;
            Q0=makeQuery(id+"F49.opExtrude","SWEPT_EDGE",EDGE,{"disambiguationData":[OSD([sQuery(id+"F48.wireOp",EDGE,"E38.0"),sQuery(id+"F48.wireOp",EDGE,"E42")])]});
            var Q1;
            Q1=makeQuery(id+"F49.opExtrude","SWEPT_EDGE",EDGE,{"disambiguationData":[OSD([sQuery(id+"F48.wireOp",EDGE,"E38.0"),sQuery(id+"F48.wireOp",EDGE,"E40")])]});
            var Q2;
            Q2=makeQuery(id+"F49.opExtrude","SWEPT_EDGE",EDGE,{"disambiguationData":[OSD([sQuery(id+"F48.wireOp",EDGE,"E39.0"),sQuery(id+"F48.wireOp",EDGE,"E42")])]});
            var Q3;
            Q3=makeQuery(id+"F49.opExtrude","SWEPT_EDGE",EDGE,{"disambiguationData":[OSD([sQuery(id+"F48.wireOp",EDGE,"E39.0"),sQuery(id+"F48.wireOp",EDGE,"E41")])]});
            fillet(context, id + "F50", {"entities" : qUnion([Q0, Q1, Q2, Q3]), "radius" : 10 * mm, "tangentPropagation" : true, "allowEdgeOverflow" : false});
        }
        {
            var Q0;
            Q0=makeQuery(id+"F49.opExtrude","CAP_FACE",FACE,{"disambiguationData":[OSD([sQuery(id+"F48.wireOp",EDGE,"E38.0"),sQuery(id+"F48.wireOp",EDGE,"E39.0"),sQuery(id+"F48.wireOp",EDGE,"E40"),sQuery(id+"F48.wireOp",EDGE,"E41"),sQuery(id+"F48.wireOp",EDGE,"E42")])],"isStart":false});
            var sketch = newSketch(context, id + "F51", { "sketchPlane" : qUnion([Q0])});
            skLineSegment(sketch, "E43", {"start": v(-45, 50) * mm, "end": v(-30, 50) * mm, "construction": true});
            skLineSegment(sketch, "E44", {"start": v(60, 50) * mm, "end": v(45, 50) * mm, "construction": true});
            skSolve(sketch);
        }
        {
            var Q0;
            Q0=sQuery(id+"F51.wireOp",VERTEX,"E43.end");
            var Q1;
            Q1=sQuery(id+"F51.wireOp",VERTEX,"E44.end");
            var Q2;
            Q2=makeQuery(id+"F40.opExtrude","SWEPT_BODY",BODY,{"disambiguationData":[OSD([sQuery(id+"F39.wireOp",EDGE,"E35.bottom"),sQuery(id+"F39.wireOp",EDGE,"E35.top"),sQuery(id+"F39.wireOp",EDGE,"E35.left"),sQuery(id+"F39.wireOp",EDGE,"E35.right")])]});
            var Q3;
            Q3=makeQuery(id+"F49.opExtrude","SWEPT_BODY",BODY,{"disambiguationData":[OSD([sQuery(id+"F48.wireOp",EDGE,"E38.0"),sQuery(id+"F48.wireOp",EDGE,"E39.0"),sQuery(id+"F48.wireOp",EDGE,"E40"),sQuery(id+"F48.wireOp",EDGE,"E41"),sQuery(id+"F48.wireOp",EDGE,"E42")])]});
            hole(context, id + "F52", {"style" : HoleStyle.SIMPLE, "endStyle" : HoleEndStyle.THROUGH, "holeDiameter" : 4 * mm, "majorDiameter" : 5 * mm, "isTappedThrough" : true, "tappedDepth" : 12 * mm, "tapClearance" : 3, "locations" : qUnion([Q0, Q1]), "scope" : qUnion([Q2, Q3])});
        }
        {
            var Q0;
            Q0=makeQuery(id+"F45.boolean.opBoolean","MERGE",FACE,{"derivedFrom":[makeQuery(id+"F40.opExtrude","SWEPT_FACE",FACE,{"disambiguationData":[OSD([sQuery(id+"F39.wireOp",EDGE,"E35.bottom")])]}),makeQuery(id+"F45.opExtrude","SWEPT_FACE",FACE,{"disambiguationData":[OSD([sQuery(id+"F44.wireOp",EDGE,"E37.left")])]})]});
            var sketch = newSketch(context, id + "F53", { "sketchPlane" : qUnion([Q0])});
            skLineSegment(sketch, "E45.bottom", {"start": v(48, 40) * mm, "end": v(42, 40) * mm});
            skLineSegment(sketch, "E45.top", {"start": v(48, 60) * mm, "end": v(42, 60) * mm});
            skLineSegment(sketch, "E45.left", {"start": v(48, 40) * mm, "end": v(48, 60) * mm});
            skLineSegment(sketch, "E45.right", {"start": v(42, 40) * mm, "end": v(42, 60) * mm});
            skPoint(sketch, "E45.middle", {"position": v(45, 50) * mm});
            skLineSegment(sketch, "E46.bottom", {"start": v(-33, 40) * mm, "end": v(-27, 40) * mm});
            skLineSegment(sketch, "E46.top", {"start": v(-33, 60) * mm, "end": v(-27, 60) * mm});
            skLineSegment(sketch, "E46.left", {"start": v(-33, 40) * mm, "end": v(-33, 60) * mm});
            skLineSegment(sketch, "E46.right", {"start": v(-27, 40) * mm, "end": v(-27, 60) * mm});
            skPoint(sketch, "E46.middle", {"position": v(-30, 50) * mm});
            skSolve(sketch);
        }
        {
            var Q0;
            Q0 = qSketchRegion(id + "F53", true);
            var Q1;
            Q1=makeQuery(id+"F49.opExtrude","CAP_FACE",FACE,{"disambiguationData":[OSD([sQuery(id+"F48.wireOp",EDGE,"E38.0"),sQuery(id+"F48.wireOp",EDGE,"E39.0"),sQuery(id+"F48.wireOp",EDGE,"E40"),sQuery(id+"F48.wireOp",EDGE,"E41"),sQuery(id+"F48.wireOp",EDGE,"E42")])],"isStart":true});
            extrude(context, id + "F54", {"entities" : qUnion([Q0]), "endBound" : BoundingType.UP_TO_SURFACE, "depth" : 25 * mm, "endBoundEntityFace" : qUnion([Q1]), "offsetDistance" : 25 * mm});
        }
        {
            var Q0;
            Q0=sQuery(id+"F51.wireOp",VERTEX,"E43.end");
            var Q1;
            Q1=sQuery(id+"F51.wireOp",VERTEX,"E44.end");
            var Q2;
            Q2=makeQuery(id+"F54.opExtrude","SWEPT_BODY",BODY,{"disambiguationData":[OSD([sQuery(id+"F53.wireOp",EDGE,"E46.bottom"),sQuery(id+"F53.wireOp",EDGE,"E46.top"),sQuery(id+"F53.wireOp",EDGE,"E46.left"),sQuery(id+"F53.wireOp",EDGE,"E46.right")])]});
            var Q3;
            Q3=makeQuery(id+"F54.opExtrude","SWEPT_BODY",BODY,{"disambiguationData":[OSD([sQuery(id+"F53.wireOp",EDGE,"E45.bottom"),sQuery(id+"F53.wireOp",EDGE,"E45.top"),sQuery(id+"F53.wireOp",EDGE,"E45.left"),sQuery(id+"F53.wireOp",EDGE,"E45.right")])]});
            hole(context, id + "F55", {"style" : HoleStyle.SIMPLE, "endStyle" : HoleEndStyle.THROUGH, "holeDiameter" : 4 * mm, "majorDiameter" : 5 * mm, "isTappedThrough" : true, "tappedDepth" : 12 * mm, "tapClearance" : 3, "locations" : qUnion([Q0, Q1]), "scope" : qUnion([Q2, Q3])});
        }
        {
            var Q0;
            Q0=sQuery(id+"F51.wireOp",VERTEX,"E44.start");
            var Q1;
            Q1=makeQuery(id+"F49.opExtrude","SWEPT_BODY",BODY,{"disambiguationData":[OSD([sQuery(id+"F48.wireOp",EDGE,"E38.0"),sQuery(id+"F48.wireOp",EDGE,"E39.0"),sQuery(id+"F48.wireOp",EDGE,"E40"),sQuery(id+"F48.wireOp",EDGE,"E41"),sQuery(id+"F48.wireOp",EDGE,"E42")])]});
            hole(context, id + "F56", {"style" : HoleStyle.SIMPLE, "endStyle" : HoleEndStyle.THROUGH, "holeDiameter" : 10 * mm, "majorDiameter" : 5 * mm, "isTappedThrough" : true, "tappedDepth" : 12 * mm, "tapClearance" : 3, "locations" : qUnion([Q0]), "scope" : qUnion([Q1])});
        }
        {
            var Q0;
            Q0=sQuery(id+"F51.wireOp",VERTEX,"E44.start");
            var Q1;
            Q1=makeQuery(id+"F40.opExtrude","SWEPT_BODY",BODY,{"disambiguationData":[OSD([sQuery(id+"F39.wireOp",EDGE,"E35.bottom"),sQuery(id+"F39.wireOp",EDGE,"E35.top"),sQuery(id+"F39.wireOp",EDGE,"E35.left"),sQuery(id+"F39.wireOp",EDGE,"E35.right")])]});
            hole(context, id + "F57", {"style" : HoleStyle.SIMPLE, "endStyle" : HoleEndStyle.THROUGH, "holeDiameter" : 5 * mm, "majorDiameter" : 5 * mm, "isTappedThrough" : true, "tappedDepth" : 12 * mm, "tapClearance" : 3, "locations" : qUnion([Q0]), "scope" : qUnion([Q1])});
        }
        {
            var Q0;
            {var subQ3=sQuery(id+"F0.wireOp",EDGE,"E0.bottom");Q0=makeQuery(id+"F3.imprint","IMPRINT",FACE,{"disambiguationData":[TD([[makeQuery(id+"F3.imprint","IMPRINT",EDGE,{"derivedFrom":makeQuery(id+"F1.opExtrude","CAP_EDGE",EDGE,{"disambiguationData":[OSD([subQ3])],"isStart":false})}),-1.0]])]});}
            var sketch = newSketch(context, id + "F58", { "sketchPlane" : qUnion([Q0])});
            skLineSegment(sketch, "E47.bottom", {"start": v(95, -95) * mm, "end": v(-25, -95) * mm});
            skLineSegment(sketch, "E47.top", {"start": v(95, 5) * mm, "end": v(-25, 5) * mm});
            skLineSegment(sketch, "E47.left", {"start": v(95, -95) * mm, "end": v(95, 5) * mm});
            skLineSegment(sketch, "E47.right", {"start": v(-25, -95) * mm, "end": v(-25, 5) * mm});
            skSolve(sketch);
        }
        {
            var Q0;
            Q0 = qSketchRegion(id + "F58", true);
            extrude(context, id + "F59", {"entities" : qUnion([Q0]), "depth" : 25 * mm, "offsetDistance" : 25 * mm});
        }
        {
            var Q0;
            Q0=makeQuery(id+"F59.opExtrude","CAP_FACE",FACE,{"disambiguationData":[OSD([sQuery(id+"F58.wireOp",EDGE,"E47.bottom"),sQuery(id+"F58.wireOp",EDGE,"E47.top"),sQuery(id+"F58.wireOp",EDGE,"E47.left"),sQuery(id+"F58.wireOp",EDGE,"E47.right")])],"isStart":false});
            extrude(context, id + "F60", {"entities" : qUnion([Q0]), "depth" : 3 * mm, "offsetDistance" : 25 * mm});
        }
        {
            var Q0;
            Q0=makeQuery(id+"F59.opExtrude","SWEPT_EDGE",EDGE,{"disambiguationData":[OSD([sQuery(id+"F58.wireOp",EDGE,"E47.bottom"),sQuery(id+"F58.wireOp",EDGE,"E47.left")])]});
            var Q1;
            Q1=makeQuery(id+"F60.opExtrude","SWEPT_EDGE",EDGE,{"disambiguationData":[OSD([sQuery(id+"F58.wireOp",EDGE,"E47.bottom"),sQuery(id+"F58.wireOp",EDGE,"E47.left")])]});
            var Q2;
            Q2=makeQuery(id+"F59.opExtrude","SWEPT_EDGE",EDGE,{"disambiguationData":[OSD([sQuery(id+"F58.wireOp",EDGE,"E47.bottom"),sQuery(id+"F58.wireOp",EDGE,"E47.right")])]});
            var Q3;
            Q3=makeQuery(id+"F60.opExtrude","SWEPT_EDGE",EDGE,{"disambiguationData":[OSD([sQuery(id+"F58.wireOp",EDGE,"E47.bottom"),sQuery(id+"F58.wireOp",EDGE,"E47.right")])]});
            var Q4;
            Q4=makeQuery(id+"F59.opExtrude","SWEPT_EDGE",EDGE,{"disambiguationData":[OSD([sQuery(id+"F58.wireOp",EDGE,"E47.top"),sQuery(id+"F58.wireOp",EDGE,"E47.left")])]});
            var Q5;
            Q5=makeQuery(id+"F60.opExtrude","SWEPT_EDGE",EDGE,{"disambiguationData":[OSD([sQuery(id+"F58.wireOp",EDGE,"E47.top"),sQuery(id+"F58.wireOp",EDGE,"E47.left")])]});
            var Q6;
            Q6=makeQuery(id+"F59.opExtrude","SWEPT_EDGE",EDGE,{"disambiguationData":[OSD([sQuery(id+"F58.wireOp",EDGE,"E47.top"),sQuery(id+"F58.wireOp",EDGE,"E47.right")])]});
            var Q7;
            Q7=makeQuery(id+"F60.opExtrude","SWEPT_EDGE",EDGE,{"disambiguationData":[OSD([sQuery(id+"F58.wireOp",EDGE,"E47.top"),sQuery(id+"F58.wireOp",EDGE,"E47.right")])]});
            fillet(context, id + "F61", {"entities" : qUnion([Q0, Q1, Q2, Q3, Q4, Q5, Q6, Q7]), "radius" : 5 * mm, "tangentPropagation" : true, "allowEdgeOverflow" : false});
        }
        {
            var Q0;
            Q0=makeQuery(id+"F59.opExtrude","CAP_FACE",FACE,{"disambiguationData":[OSD([sQuery(id+"F58.wireOp",EDGE,"E47.bottom"),sQuery(id+"F58.wireOp",EDGE,"E47.top"),sQuery(id+"F58.wireOp",EDGE,"E47.left"),sQuery(id+"F58.wireOp",EDGE,"E47.right")])],"isStart":false});
            shell(context, id + "F62", {"entities" : qUnion([Q0]), "thickness" : 2.5 * mm});
        }
        {
            var Q0;
            Q0=makeQuery(id+"F59.opExtrude","CAP_FACE",FACE,{"disambiguationData":[OSD([sQuery(id+"F58.wireOp",EDGE,"E47.bottom"),sQuery(id+"F58.wireOp",EDGE,"E47.top"),sQuery(id+"F58.wireOp",EDGE,"E47.left"),sQuery(id+"F58.wireOp",EDGE,"E47.right")])],"isStart":false});
            var sketch = newSketch(context, id + "F63", { "sketchPlane" : qUnion([Q0])});
            skLineSegment(sketch, "E48", {"start": v(82.5, 2.5) * mm, "end": v(82.5, -7.5) * mm});
            skLineSegment(sketch, "E49", {"start": v(82.5, -7.5) * mm, "end": v(92.5, -7.5) * mm});
            skLineSegment(sketch, "E50", {"start": v(35, 2.5) * mm, "end": v(35, -92.5) * mm, "construction": true});
            skLineSegment(sketch, "E51.MirrorCS", {"start": v(-12.5, 2.5) * mm, "end": v(-12.5, -7.5) * mm});
            skLineSegment(sketch, "E52.MirrorCS", {"start": v(-12.5, -7.5) * mm, "end": v(-22.5, -7.5) * mm});
            skLineSegment(sketch, "E53", {"start": v(-22.5, -45) * mm, "end": v(92.5, -45) * mm, "construction": true});
            skLineSegment(sketch, "E54.MirrorCS", {"start": v(82.5, -82.5) * mm, "end": v(92.5, -82.5) * mm});
            skLineSegment(sketch, "E55.MirrorCS", {"start": v(82.5, -92.5) * mm, "end": v(82.5, -82.5) * mm});
            skLineSegment(sketch, "E56.MirrorCS", {"start": v(-12.5, -82.5) * mm, "end": v(-22.5, -82.5) * mm});
            skLineSegment(sketch, "E57.MirrorCS", {"start": v(-12.5, -92.5) * mm, "end": v(-12.5, -82.5) * mm});
            skSolve(sketch);
        }
        {
            var Q0;
            {var subQ6=sQuery(id+"F63.wireOp",EDGE,"E51.MirrorCS");Q0=makeQuery(id+"F63.imprint","IMPRINT",FACE,{"disambiguationData":[TD([[makeQuery(id+"F63.imprint","IMPRINT",EDGE,{"derivedFrom":subQ6}),-1.0]])]});}
            var Q1;
            {var subQ6=sQuery(id+"F63.wireOp",EDGE,"E48");Q1=makeQuery(id+"F63.imprint","IMPRINT",FACE,{"disambiguationData":[TD([[makeQuery(id+"F63.imprint","IMPRINT",EDGE,{"derivedFrom":subQ6}),1.0]])]});}
            var Q2;
            {var subQ5=sQuery(id+"F63.wireOp",EDGE,"E56.MirrorCS");Q2=makeQuery(id+"F63.imprint","IMPRINT",FACE,{"disambiguationData":[TD([[makeQuery(id+"F63.imprint","IMPRINT",EDGE,{"derivedFrom":subQ5}),1.0]])]});}
            var Q3;
            {var subQ7=sQuery(id+"F63.wireOp",EDGE,"E54.MirrorCS");Q3=makeQuery(id+"F63.imprint","IMPRINT",FACE,{"disambiguationData":[TD([[makeQuery(id+"F63.imprint","IMPRINT",EDGE,{"derivedFrom":subQ7}),-1.0]])]});}
            extrude(context, id + "F64", {"entities" : qUnion([Q0, Q1, Q2, Q3]), "operationType" : NewBodyOperationType.ADD, "oppositeDirection" : true, "depth" : 4 * mm, "offsetDistance" : 25 * mm});
        }
        {
            var Q0;
            Q0=makeQuery(id+"F64.opExtrude","SWEPT_EDGE",EDGE,{"disambiguationData":[OSD([sQuery(id+"F63.wireOp",EDGE,"E51.MirrorCS"),sQuery(id+"F63.wireOp",EDGE,"E52.MirrorCS")])]});
            var Q1;
            Q1=makeQuery(id+"F64.opExtrude","SWEPT_EDGE",EDGE,{"disambiguationData":[OSD([sQuery(id+"F63.wireOp",EDGE,"E48"),sQuery(id+"F63.wireOp",EDGE,"E49")])]});
            var Q2;
            Q2=makeQuery(id+"F64.opExtrude","SWEPT_EDGE",EDGE,{"disambiguationData":[OSD([sQuery(id+"F63.wireOp",EDGE,"E54.MirrorCS"),sQuery(id+"F63.wireOp",EDGE,"E55.MirrorCS")])]});
            var Q3;
            Q3=makeQuery(id+"F64.opExtrude","SWEPT_EDGE",EDGE,{"disambiguationData":[OSD([sQuery(id+"F63.wireOp",EDGE,"E56.MirrorCS"),sQuery(id+"F63.wireOp",EDGE,"E57.MirrorCS")])]});
            fillet(context, id + "F65", {"entities" : qUnion([Q0, Q1, Q2, Q3]), "radius" : 5 * mm, "tangentPropagation" : true, "allowEdgeOverflow" : false});
        }
        {
            var Q0;
            {var subQ6=sQuery(id+"F63.wireOp",EDGE,"E48");Q0=makeQuery(id+"F63.imprint","IMPRINT",FACE,{"disambiguationData":[TD([[makeQuery(id+"F63.imprint","IMPRINT",EDGE,{"derivedFrom":subQ6}),1.0]])]});}
            var sketch = newSketch(context, id + "F66", { "sketchPlane" : qUnion([Q0])});
            skPoint(sketch, "E58", {"position": v(87.5, -2.5) * mm});
            skPoint(sketch, "E59.MirrorP", {"position": v(-17.5, -2.5) * mm});
            skPoint(sketch, "E60.MirrorP", {"position": v(87.5, -87.5) * mm});
            skPoint(sketch, "E61.MirrorP", {"position": v(-17.5, -87.5) * mm});
            skSolve(sketch);
        }
        {
            var Q0;
            Q0=sQuery(id+"F66.wireOp",VERTEX,"E58");
            var Q1;
            Q1=sQuery(id+"F66.wireOp",VERTEX,"E60.MirrorP");
            var Q2;
            Q2=sQuery(id+"F66.wireOp",VERTEX,"E61.MirrorP");
            var Q3;
            Q3=sQuery(id+"F66.wireOp",VERTEX,"E59.MirrorP");
            var Q4;
            Q4=makeQuery(id+"F1.opExtrude","SWEPT_BODY",BODY,{"disambiguationData":[OSD([sQuery(id+"F0.wireOp",EDGE,"E0.bottom"),sQuery(id+"F0.wireOp",EDGE,"E0.top"),sQuery(id+"F0.wireOp",EDGE,"E0.left"),sQuery(id+"F0.wireOp",EDGE,"E0.right")])]});
            var Q5;
            Q5=makeQuery(id+"F7.opRevolve","SWEPT_BODY",BODY,{"disambiguationData":[OSD([sQuery(id+"F6.wireOp",EDGE,"E3"),sQuery(id+"F6.wireOp",EDGE,"E4"),sQuery(id+"F6.wireOp",EDGE,"E5"),sQuery(id+"F6.wireOp",EDGE,"E6")])]});
            var Q6;
            Q6=makeQuery(id+"F59.opExtrude","SWEPT_BODY",BODY,{"disambiguationData":[OSD([sQuery(id+"F58.wireOp",EDGE,"E47.bottom"),sQuery(id+"F58.wireOp",EDGE,"E47.top"),sQuery(id+"F58.wireOp",EDGE,"E47.left"),sQuery(id+"F58.wireOp",EDGE,"E47.right")])]});
            hole(context, id + "F67", {"style" : HoleStyle.SIMPLE, "endStyle" : HoleEndStyle.THROUGH, "holeDiameter" : 2 * mm, "majorDiameter" : 5 * mm, "isTappedThrough" : true, "tappedDepth" : 12 * mm, "tapClearance" : 3, "locations" : qUnion([Q0, Q1, Q2, Q3]), "scope" : qUnion([Q4, Q5, Q6])});
        }
        {
            var Q0;
            Q0=makeQuery(id+"F19.opRevolve","SWEPT_FACE",FACE,{"disambiguationData":[OSD([sQuery(id+"F18.wireOp",EDGE,"E15")])]});
            cPlane(context, id + "F68", {"entities" : qUnion([Q0]), "cplaneType" : CPlaneType.OFFSET, "offset" : 65 * mm, "width" : 150 * mm, "height" : 150 * mm});
        }
        {
            var Q0;
            Q0=qCreatedBy(id+"F68.planeOp",FACE);
            var sketch = newSketch(context, id + "F69", { "sketchPlane" : qUnion([Q0])});
            skArc(sketch, "E62", {"start": v(77.4, 68.18) * mm, "mid": v(60, 87.5) * mm, "end": v(42.6, 68.18) * mm});
            skLineSegment(sketch, "E63", {"start": v(88, 20) * mm, "end": v(32, 20) * mm});
            skLineSegment(sketch, "E64", {"start": v(32, 20) * mm, "end": v(32, 26) * mm});
            skLineSegment(sketch, "E65", {"start": v(88, 20) * mm, "end": v(88, 26) * mm});
            skLineSegment(sketch, "E66", {"start": v(32, 26) * mm, "end": v(47, 26) * mm});
            skLineSegment(sketch, "E67", {"start": v(88, 26) * mm, "end": v(73, 26) * mm});
            skLineSegment(sketch, "E68", {"start": v(47, 26) * mm, "end": v(42.6, 68.18) * mm});
            skLineSegment(sketch, "E69", {"start": v(73, 26) * mm, "end": v(77.4, 68.18) * mm});
            skSolve(sketch);
        }
        {
            var Q0;
            Q0 = qSketchRegion(id + "F69", true);
            extrude(context, id + "F70", {"entities" : qUnion([Q0]), "endBound" : BoundingType.SYMMETRIC, "depth" : 10 * mm, "offsetDistance" : 25 * mm});
        }
        {
            var Q0;
            Q0=sQuery(id+"F14.wireOp",VERTEX,"E8.middle");
            var Q1;
            Q1=makeQuery(id+"F70.opExtrude","SWEPT_BODY",BODY,{"disambiguationData":[OSD([sQuery(id+"F69.wireOp",EDGE,"E62"),sQuery(id+"F69.wireOp",EDGE,"E63"),sQuery(id+"F69.wireOp",EDGE,"E64"),sQuery(id+"F69.wireOp",EDGE,"E65"),sQuery(id+"F69.wireOp",EDGE,"E66"),sQuery(id+"F69.wireOp",EDGE,"E67"),sQuery(id+"F69.wireOp",EDGE,"E68"),sQuery(id+"F69.wireOp",EDGE,"E69")])]});
            hole(context, id + "F71", {"style" : HoleStyle.SIMPLE, "endStyle" : HoleEndStyle.THROUGH, "oppositeDirection" : true, "holeDiameter" : 15 * mm, "majorDiameter" : 5 * mm, "isTappedThrough" : true, "tappedDepth" : 12 * mm, "tapClearance" : 3, "locations" : qUnion([Q0]), "scope" : qUnion([Q1])});
        }
        {
            var Q0;
            Q0=makeQuery(id+"F70.opExtrude","CAP_FACE",FACE,{"disambiguationData":[OSD([sQuery(id+"F69.wireOp",EDGE,"E62"),sQuery(id+"F69.wireOp",EDGE,"E63"),sQuery(id+"F69.wireOp",EDGE,"E64"),sQuery(id+"F69.wireOp",EDGE,"E65"),sQuery(id+"F69.wireOp",EDGE,"E66"),sQuery(id+"F69.wireOp",EDGE,"E67"),sQuery(id+"F69.wireOp",EDGE,"E68"),sQuery(id+"F69.wireOp",EDGE,"E69")])],"isStart":false});
            var sketch = newSketch(context, id + "F72", { "sketchPlane" : qUnion([Q0])});
            skLineSegment(sketch, "E70.bottom", {"start": v(90, 75) * mm, "end": v(65.6, 75) * mm});
            skLineSegment(sketch, "E70.top", {"start": v(90, 65) * mm, "end": v(65.6, 65) * mm});
            skLineSegment(sketch, "E70.left", {"start": v(90, 75) * mm, "end": v(90, 65) * mm});
            skPoint(sketch, "E70.middle", {"position": v(60, 70) * mm});
            skPoint(sketch, "E70.right.start.orphan", {"position": v(30, 75) * mm});
            skPoint(sketch, "E71.orphan", {"position": v(30, 65) * mm});
            skCircle(sketch, "E72", {"center": v(60, 70) * mm, "radius": 7.5 * mm});
            skPoint(sketch, "E73.orphan", {"position": v(60, 75) * mm});
            skPoint(sketch, "E74.start.orphan", {"position": v(60, 65) * mm});
            skSolve(sketch);
        }
        {
            var Q0;
            {var subQ5=sQuery(id+"F72.wireOp",EDGE,"E70.left");Q0=makeQuery(id+"F72.imprint","IMPRINT",FACE,{"disambiguationData":[TD([[makeQuery(id+"F72.imprint","IMPRINT",EDGE,{"derivedFrom":subQ5}),-1.0]])]});}
            var Q1;
            Q1=makeQuery(id+"F70.opExtrude","CAP_FACE",FACE,{"disambiguationData":[OSD([sQuery(id+"F69.wireOp",EDGE,"E62"),sQuery(id+"F69.wireOp",EDGE,"E63"),sQuery(id+"F69.wireOp",EDGE,"E64"),sQuery(id+"F69.wireOp",EDGE,"E65"),sQuery(id+"F69.wireOp",EDGE,"E66"),sQuery(id+"F69.wireOp",EDGE,"E67"),sQuery(id+"F69.wireOp",EDGE,"E68"),sQuery(id+"F69.wireOp",EDGE,"E69")])],"isStart":true});
            extrude(context, id + "F73", {"entities" : qUnion([Q0]), "operationType" : NewBodyOperationType.ADD, "endBound" : BoundingType.UP_TO_SURFACE, "oppositeDirection" : true, "depth" : 25 * mm, "endBoundEntityFace" : qUnion([Q1]), "offsetDistance" : 25 * mm});
        }
        {
            var Q0;
            {var subQ0=sQuery(id+"F69.wireOp",EDGE,"E69");var subQ1=sQuery(id+"F69.wireOp",EDGE,"E62");Q0=makeQuery(id+"F73.boolean.opBoolean","MERGE",FACE,{"derivedFrom":[makeQuery(id+"F70.opExtrude","CAP_FACE",FACE,{"disambiguationData":[OSD([subQ1,sQuery(id+"F69.wireOp",EDGE,"E63"),sQuery(id+"F69.wireOp",EDGE,"E64"),sQuery(id+"F69.wireOp",EDGE,"E65"),sQuery(id+"F69.wireOp",EDGE,"E66"),sQuery(id+"F69.wireOp",EDGE,"E67"),sQuery(id+"F69.wireOp",EDGE,"E68"),subQ0])],"isStart":false}),makeQuery(id+"F73.opExtrude","CAP_FACE",FACE,{"disambiguationData":[OSD([subQ1,subQ0,sQuery(id+"F72.wireOp",EDGE,"E70.bottom"),sQuery(id+"F72.wireOp",EDGE,"E70.top"),sQuery(id+"F72.wireOp",EDGE,"E70.left")])],"isStart":true})]});}
            var sketch = newSketch(context, id + "F74", { "sketchPlane" : qUnion([Q0])});
            skLineSegment(sketch, "E75.bottom", {"start": v(100.89, 70.75) * mm, "end": v(65.89, 70.75) * mm});
            skLineSegment(sketch, "E75.top", {"start": v(100.89, 69.25) * mm, "end": v(65.89, 69.25) * mm});
            skLineSegment(sketch, "E75.left", {"start": v(100.89, 70.75) * mm, "end": v(100.89, 69.25) * mm});
            skLineSegment(sketch, "E75.right", {"start": v(65.89, 70.75) * mm, "end": v(65.89, 69.25) * mm});
            skPoint(sketch, "E75.middle", {"position": v(83.39, 70) * mm});
            skPoint(sketch, "E75.middle.positionSnap0", {"position": v(83.39, 75) * mm});
            skPoint(sketch, "E75.middle.positionSnap1", {"position": v(90, 70) * mm});
            skPoint(sketch, "E75.centerSnap0", {"position": v(83.39, 75) * mm});
            skPoint(sketch, "E75.centerSnap1", {"position": v(90, 70) * mm});
            skSolve(sketch);
        }
        {
            var Q0;
            Q0 = qSketchRegion(id + "F74", true);
            var Q1;
            {var subQ0=sQuery(id+"F69.wireOp",EDGE,"E69");var subQ1=sQuery(id+"F69.wireOp",EDGE,"E68");var subQ2=sQuery(id+"F69.wireOp",EDGE,"E67");var subQ3=sQuery(id+"F69.wireOp",EDGE,"E66");var subQ4=sQuery(id+"F69.wireOp",EDGE,"E65");var subQ5=sQuery(id+"F69.wireOp",EDGE,"E64");var subQ6=sQuery(id+"F69.wireOp",EDGE,"E63");var subQ7=sQuery(id+"F69.wireOp",EDGE,"E62");Q1=makeQuery(id+"F73.boolean.opBoolean","MERGE",FACE,{"derivedFrom":[makeQuery(id+"F70.opExtrude","CAP_FACE",FACE,{"disambiguationData":[OSD([subQ7,subQ6,subQ5,subQ4,subQ3,subQ2,subQ1,subQ0])],"isStart":true}),makeQuery(id+"F73.opExtrude","CAP_FACE",FACE,{"disambiguationData":[OSD([subQ7,subQ6,subQ5,subQ4,subQ3,subQ2,subQ1,subQ0])],"isStart":false})]});}
            extrude(context, id + "F75", {"entities" : qUnion([Q0]), "operationType" : NewBodyOperationType.REMOVE, "endBound" : BoundingType.UP_TO_SURFACE, "oppositeDirection" : true, "depth" : 25 * mm, "endBoundEntityFace" : qUnion([Q1]), "offsetDistance" : 25 * mm});
        }
        {
            var Q0;
            Q0=makeQuery(id+"F73.opExtrude","SWEPT_EDGE",EDGE,{"disambiguationData":[OSD([sQuery(id+"F69.wireOp",EDGE,"E62"),sQuery(id+"F72.wireOp",EDGE,"E70.bottom")])]});
            var Q1;
            Q1=makeQuery(id+"F73.opExtrude","SWEPT_EDGE",EDGE,{"disambiguationData":[OSD([sQuery(id+"F72.wireOp",EDGE,"E70.bottom"),sQuery(id+"F72.wireOp",EDGE,"E70.left")])]});
            var Q2;
            Q2=makeQuery(id+"F73.opExtrude","SWEPT_EDGE",EDGE,{"disambiguationData":[OSD([sQuery(id+"F69.wireOp",EDGE,"E69"),sQuery(id+"F72.wireOp",EDGE,"E70.top")])]});
            var Q3;
            Q3=makeQuery(id+"F73.opExtrude","SWEPT_EDGE",EDGE,{"disambiguationData":[OSD([sQuery(id+"F72.wireOp",EDGE,"E70.top"),sQuery(id+"F72.wireOp",EDGE,"E70.left")])]});
            fillet(context, id + "F76", {"entities" : qUnion([Q0, Q1, Q2, Q3]), "radius" : 2.5 * mm, "tangentPropagation" : true, "allowEdgeOverflow" : false});
        }
        {
            var Q0;
            Q0=makeQuery(id+"F73.opExtrude","SWEPT_FACE",FACE,{"disambiguationData":[OSD([sQuery(id+"F72.wireOp",EDGE,"E70.bottom")])]});
            var sketch = newSketch(context, id + "F77", { "sketchPlane" : qUnion([Q0])});
            skPoint(sketch, "E76", {"position": v(35.5, 83.02) * mm});
            skPoint(sketch, "E76.positionSnap0", {"position": v(35.5, 87.5) * mm});
            skPoint(sketch, "E76.positionSnap1", {"position": v(30.5, 83.02) * mm});
            skSolve(sketch);
        }
        {
            var Q0;
            Q0=sQuery(id+"F77.wireOp",VERTEX,"E76");
            var Q1;
            Q1=makeQuery(id+"F70.opExtrude","SWEPT_BODY",BODY,{"disambiguationData":[OSD([sQuery(id+"F69.wireOp",EDGE,"E62"),sQuery(id+"F69.wireOp",EDGE,"E63"),sQuery(id+"F69.wireOp",EDGE,"E64"),sQuery(id+"F69.wireOp",EDGE,"E65"),sQuery(id+"F69.wireOp",EDGE,"E66"),sQuery(id+"F69.wireOp",EDGE,"E67"),sQuery(id+"F69.wireOp",EDGE,"E68"),sQuery(id+"F69.wireOp",EDGE,"E69")])]});
            hole(context, id + "F78", {"style" : HoleStyle.SIMPLE, "endStyle" : HoleEndStyle.BLIND, "holeDiameter" : 2 * mm, "majorDiameter" : 5 * mm, "holeDepth" : 10 * mm, "isTappedThrough" : true, "tappedDepth" : 12 * mm, "tapClearance" : 3, "locations" : qUnion([Q0]), "scope" : qUnion([Q1])});
        }
        {
            var Q0;
            Q0=makeQuery(id+"F73.opExtrude","SWEPT_FACE",FACE,{"disambiguationData":[OSD([sQuery(id+"F72.wireOp",EDGE,"E70.bottom")])]});
            var sketch = newSketch(context, id + "F79", { "sketchPlane" : qUnion([Q0])});
            skCircle(sketch, "E77", {"center": v(35.5, 83.02) * mm, "radius": 2 * mm});
            skSolve(sketch);
        }
        {
            var Q0;
            Q0 = qSketchRegion(id + "F79", true);
            extrude(context, id + "F80", {"entities" : qUnion([Q0]), "depth" : 2 * mm, "offsetDistance" : 25 * mm});
        }
        {
            var Q0;
            Q0=makeQuery(id+"F80.opExtrude","CAP_FACE",FACE,{"disambiguationData":[OSD([sQuery(id+"F79.wireOp",EDGE,"E77")])],"isStart":false});
            var sketch = newSketch(context, id + "F81", { "sketchPlane" : qUnion([Q0])});
            skCircle(sketch, "E78", {"center": v(35.5, 83.02) * mm, "radius": 3.75 * mm});
            skSolve(sketch);
        }
        {
            var Q0;
            Q0 = qSketchRegion(id + "F81", true);
            extrude(context, id + "F82", {"entities" : qUnion([Q0]), "operationType" : NewBodyOperationType.ADD, "depth" : 2 * mm, "offsetDistance" : 25 * mm});
        }
        {
            var Q0;
            Q0=makeQuery(id+"F82.opExtrude","CAP_EDGE",EDGE,{"disambiguationData":[OSD([sQuery(id+"F81.wireOp",EDGE,"E78")])],"isStart":false});
            fillet(context, id + "F83", {"entities" : qUnion([Q0]), "radius" : 1 * mm, "tangentPropagation" : true, "allowEdgeOverflow" : false});
        }
    });
